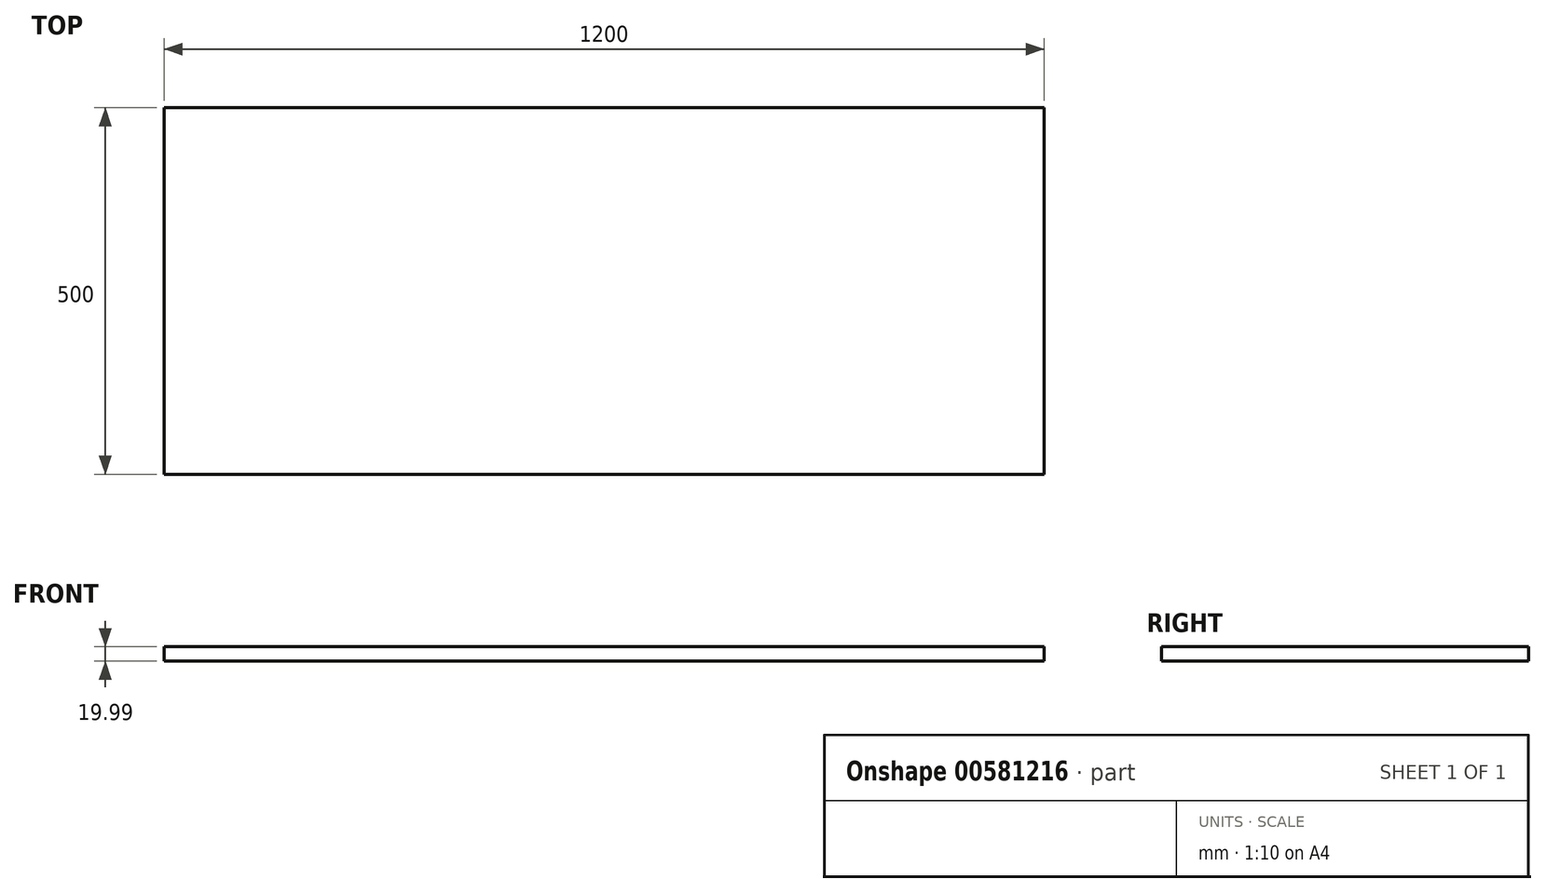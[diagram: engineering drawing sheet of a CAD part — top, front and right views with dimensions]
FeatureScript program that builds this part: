
annotation { "Feature Type Name" : "Feature", "Feature Type Description" : "" }
export const myFeature = defineFeature(function(context is Context, id is Id, definition is map)
    precondition{}
    {
        {
            var Q0;
            Q0=qCreatedBy(makeId("Top.planeOp"),FACE);
            var sketch = newSketch(context, id + "F0", { "sketchPlane" : qUnion([Q0])});
            skLineSegment(sketch, "E0.bottom", {"start": v(668.3, 233.56) * mm, "end": v(-531.7, 233.56) * mm});
            skLineSegment(sketch, "E0.top", {"start": v(668.3, -266.44) * mm, "end": v(-531.7, -266.44) * mm});
            skLineSegment(sketch, "E0.left", {"start": v(668.3, 233.56) * mm, "end": v(668.3, -266.44) * mm});
            skLineSegment(sketch, "E0.right", {"start": v(-531.7, 233.56) * mm, "end": v(-531.7, -266.44) * mm});
            skPoint(sketch, "E0.middle", {"position": v(68.3, -16.44) * mm});
            skSolve(sketch);
        }
        {
            var Q0;
            Q0=qSketchRegion(id+"F0",true);
            extrude(context, id + "F1", {"entities" : qUnion([Q0]), "depth" : 19.99 * mm, "offsetDistance" : 25.4 * mm});
        }
    });
